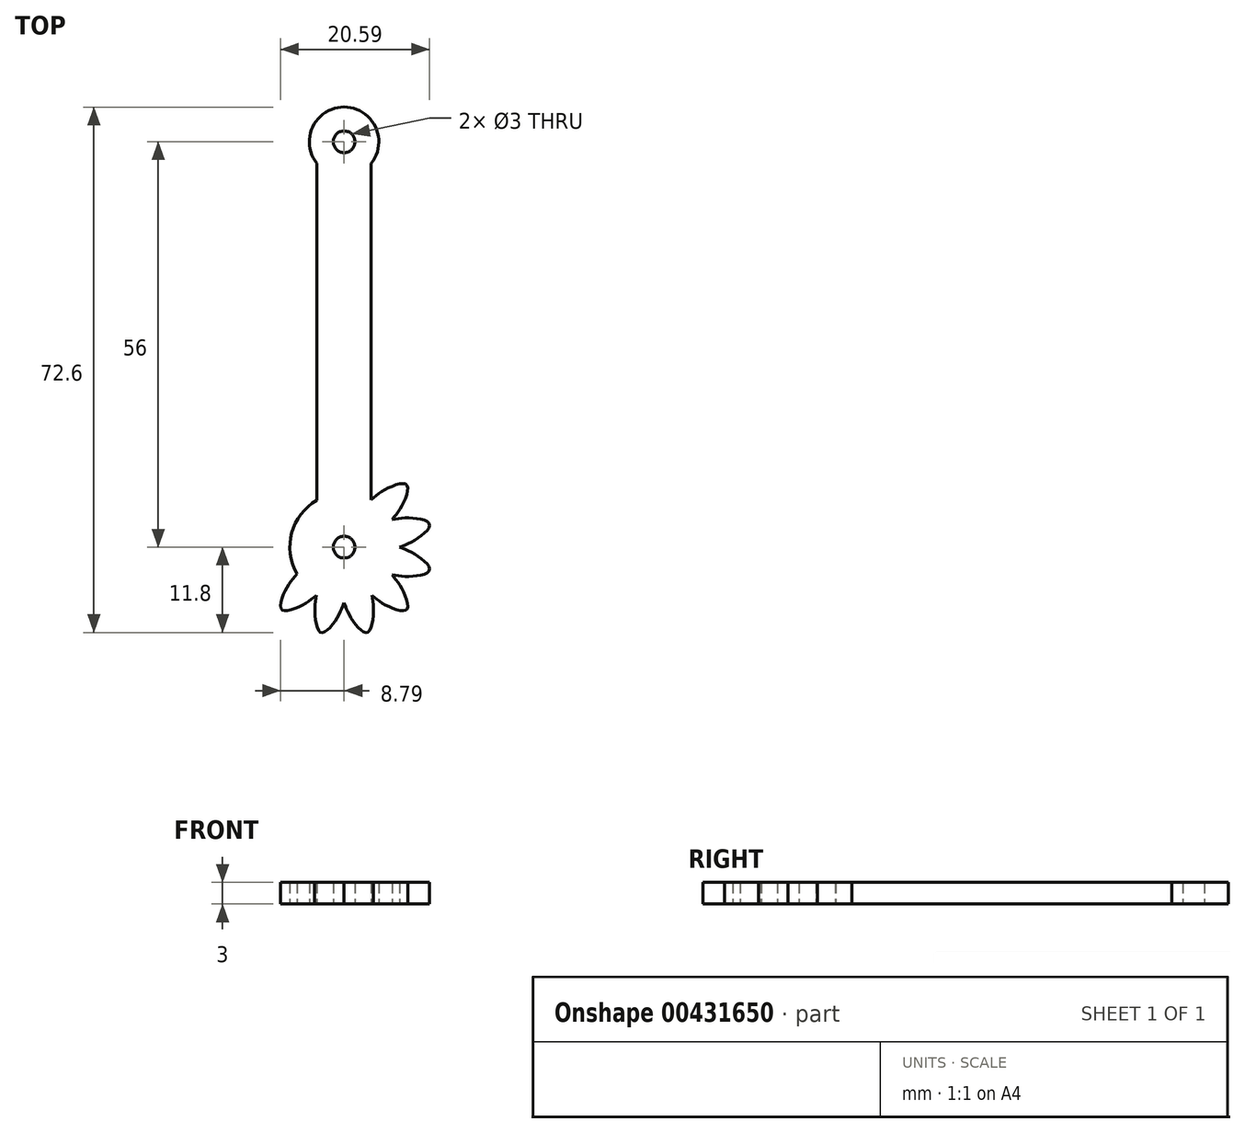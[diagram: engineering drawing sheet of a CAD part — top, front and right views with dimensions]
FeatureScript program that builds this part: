
annotation { "Feature Type Name" : "Feature", "Feature Type Description" : "" }
export const myFeature = defineFeature(function(context is Context, id is Id, definition is map)
    precondition{}
    {
        {
            var Q0;
            Q0=qCreatedBy(makeId("Top.planeOp"),FACE);
            var sketch = newSketch(context, id + "F0", { "sketchPlane" : qUnion([Q0])});
            skLineSegment(sketch, "E0.bottom", {"start": v(0, 0) * mm, "end": v(0, 0) * mm});
            skLineSegment(sketch, "E0.top", {"start": v(0, 50) * mm, "end": v(7.5, 50) * mm, "construction": true});
            skLineSegment(sketch, "E0.left", {"start": v(0, 0) * mm, "end": v(0, 0) * mm});
            skLineSegment(sketch, "E0.right", {"start": v(7.5, 0) * mm, "end": v(7.5, 0) * mm});
            skLineSegment(sketch, "E1", {"start": v(3.75, 50) * mm, "end": v(3.75, 53) * mm, "construction": true});
            skLineSegment(sketch, "E2", {"start": v(3.75, 0) * mm, "end": v(3.75, -3) * mm, "construction": true});
            skCircle(sketch, "E3", {"center": v(3.75, -3) * mm, "radius": 1.5 * mm});
            skCircle(sketch, "E4", {"center": v(3.75, 53) * mm, "radius": 1.5 * mm});
            skArc(sketch, "E5", {"start": v(0, 50) * mm, "mid": v(3.75, 48.2) * mm, "end": v(7.5, 50) * mm, "construction": true});
            skArc(sketch, "E6", {"start": v(7.5, 50) * mm, "mid": v(3.75, 57.8) * mm, "end": v(0, 50) * mm});
            skLineSegment(sketch, "E7", {"start": v(0, 0) * mm, "end": v(0, 50) * mm});
            skLineSegment(sketch, "E8", {"start": v(0, 0) * mm, "end": v(7.5, 0) * mm, "construction": true});
            skLineSegment(sketch, "E9", {"start": v(7.5, 0) * mm, "end": v(7.5, 50) * mm});
            skCircle(sketch, "E10", {"center": v(3.75, -3) * mm, "radius": 7.5 * mm});
            skLineSegment(sketch, "E11.bottom", {"start": v(3.75, -3) * mm, "end": v(6.75, -3) * mm});
            skLineSegment(sketch, "E12", {"start": v(9.05, -8.3) * mm, "end": v(7.64, -9.72) * mm, "construction": true});
            skLineSegment(sketch, "E13", {"start": v(7.64, -9.72) * mm, "end": v(7.45, -9.53) * mm});
            skLineSegment(sketch, "E14", {"start": v(10.47, -6.89) * mm, "end": v(10.28, -6.7) * mm});
            skLineSegment(sketch, "E15", {"start": v(10.82, -10.07) * mm, "end": v(11.88, -9.01) * mm, "construction": true});
            skLineSegment(sketch, "E16", {"start": v(11.88, -9.01) * mm, "end": v(9.76, -11.13) * mm, "construction": true});
            skFitSpline(sketch, "E17", {"points": [v(10.28, -6.7) * mm, v(11.88, -9.01) * mm, v(12.38, -11.63) * mm, v(9.76, -11.13) * mm, v(7.45, -9.53) * mm], "startDerivative": vector(6.57, -7.89) * mm, "endDerivative": vector(-7.89, 6.57) * mm});
            skSolve(sketch);
        }
        {
            var Q0;
            Q0=makeQuery(id+"F0.imprint","IMPRINT",FACE,{"disambiguationData":[TD([[makeQuery(id+"F0.imprint","IMPRINT",EDGE,{"derivedFrom":sQuery(id+"F0.wireOp",EDGE,"E3")}),-1.0]])]});
            var Q1;
            {var subQ0=sQuery(id+"F0.wireOp",EDGE,"E17");Q1=makeQuery(id+"F0.imprint","IMPRINT",FACE,{"disambiguationData":[TD([[makeQuery(id+"F0.imprint","IMPRINT",EDGE,{"derivedFrom":subQ0}),-1.0]])]});}
            extrude(context, id + "F1", {"entities" : qUnion([Q0, Q1]), "depth" : 3 * mm});
        }
        {
            var Q0;
            Q0=makeQuery(id+"F1.opExtrude","SWEPT_BODY",BODY,{"disambiguationData":[OSD([sQuery(id+"F0.wireOp",EDGE,"E3"),sQuery(id+"F0.wireOp",EDGE,"E10"),sQuery(id+"F0.wireOp",EDGE,"E17")])]});
            var Q1;
            Q1=sQuery(id+"F0.wireOp",EDGE,"E3");
            circularPattern(context, id + "F2", {"operationType" : NewBodyOperationType.ADD, "entities" : qUnion([Q0]), "axis" : qUnion([Q1]), "angle" : 90 * degree, "instanceCount" : 4, "equalSpace" : true, "isCentered" : true});
        }
        {
            var Q0;
            Q0=makeQuery(id+"F0.imprint","IMPRINT",FACE,{"disambiguationData":[TD([[makeQuery(id+"F0.imprint","IMPRINT",EDGE,{"derivedFrom":sQuery(id+"F0.wireOp",EDGE,"E4")}),-1.0]])]});
            extrude(context, id + "F3", {"entities" : qUnion([Q0]), "operationType" : NewBodyOperationType.ADD, "depth" : 3 * mm});
        }
    });
